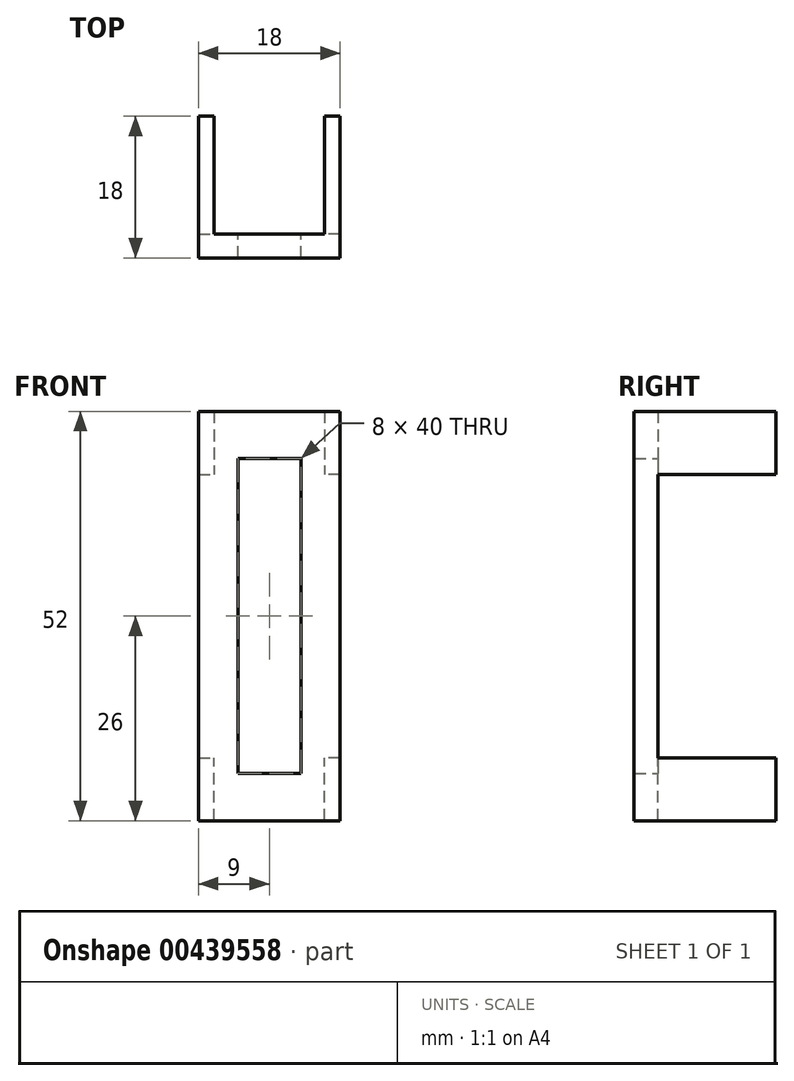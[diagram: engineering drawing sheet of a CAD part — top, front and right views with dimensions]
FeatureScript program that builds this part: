
annotation { "Feature Type Name" : "Feature", "Feature Type Description" : "" }
export const myFeature = defineFeature(function(context is Context, id is Id, definition is map)
    precondition{}
    {
        {
            var Q0;
            Q0=qCreatedBy(makeId("Front.planeOp"),FACE);
            var sketch = newSketch(context, id + "F0", { "sketchPlane" : qUnion([Q0])});
            skLineSegment(sketch, "E0.bottom", {"start": v(-9, 26) * mm, "end": v(9, 26) * mm});
            skLineSegment(sketch, "E0.top", {"start": v(-9, -26) * mm, "end": v(9, -26) * mm});
            skLineSegment(sketch, "E0.left", {"start": v(-9, 26) * mm, "end": v(-9, -26) * mm});
            skLineSegment(sketch, "E0.right", {"start": v(9, 26) * mm, "end": v(9, -26) * mm});
            skLineSegment(sketch, "E1.bottom", {"start": v(-4, 20) * mm, "end": v(4, 20) * mm});
            skLineSegment(sketch, "E1.top", {"start": v(-4, -20) * mm, "end": v(4, -20) * mm});
            skLineSegment(sketch, "E1.left", {"start": v(-4, 20) * mm, "end": v(-4, -20) * mm});
            skLineSegment(sketch, "E1.right", {"start": v(4, 20) * mm, "end": v(4, -20) * mm});
            skSolve(sketch);
        }
        {
            var Q0;
            Q0=makeQuery(id+"F0.imprint","IMPRINT",FACE,{"disambiguationData":[TD([[makeQuery(id+"F0.imprint","IMPRINT",EDGE,{"derivedFrom":sQuery(id+"F0.wireOp",EDGE,"E0.bottom")}),-1.0]])]});
            extrude(context, id + "F1", {"entities" : qUnion([Q0]), "depth" : 3 * mm, "offsetDistance" : 25 * mm});
        }
        {
            var Q0;
            Q0=makeQuery(id+"F1.opExtrude","CAP_FACE",FACE,{"disambiguationData":[OSD([sQuery(id+"F0.wireOp",EDGE,"E0.bottom"),sQuery(id+"F0.wireOp",EDGE,"E0.top"),sQuery(id+"F0.wireOp",EDGE,"E0.left"),sQuery(id+"F0.wireOp",EDGE,"E0.right")])],"isStart":true});
            var sketch = newSketch(context, id + "F2", { "sketchPlane" : qUnion([Q0])});
            skLineSegment(sketch, "E2.bottom", {"start": v(-9, 26) * mm, "end": v(-7, 26) * mm});
            skLineSegment(sketch, "E2.top", {"start": v(-9, 18) * mm, "end": v(-7, 18) * mm});
            skLineSegment(sketch, "E2.left", {"start": v(-9, 26) * mm, "end": v(-9, 18) * mm});
            skLineSegment(sketch, "E2.right", {"start": v(-7, 26) * mm, "end": v(-7, 18) * mm});
            skLineSegment(sketch, "E3.bottom", {"start": v(9, 26) * mm, "end": v(7, 26) * mm});
            skLineSegment(sketch, "E3.top", {"start": v(9, 18) * mm, "end": v(7, 18) * mm});
            skLineSegment(sketch, "E3.left", {"start": v(9, 26) * mm, "end": v(9, 18) * mm});
            skLineSegment(sketch, "E3.right", {"start": v(7, 26) * mm, "end": v(7, 18) * mm});
            skLineSegment(sketch, "E4.bottom", {"start": v(9, -26) * mm, "end": v(7, -26) * mm});
            skLineSegment(sketch, "E4.top", {"start": v(9, -18) * mm, "end": v(7, -18) * mm});
            skLineSegment(sketch, "E4.left", {"start": v(9, -26) * mm, "end": v(9, -18) * mm});
            skLineSegment(sketch, "E4.right", {"start": v(7, -26) * mm, "end": v(7, -18) * mm});
            skLineSegment(sketch, "E5.bottom", {"start": v(-9, -26) * mm, "end": v(-7, -26) * mm});
            skLineSegment(sketch, "E5.top", {"start": v(-9, -18) * mm, "end": v(-7, -18) * mm});
            skLineSegment(sketch, "E5.left", {"start": v(-9, -26) * mm, "end": v(-9, -18) * mm});
            skLineSegment(sketch, "E5.right", {"start": v(-7, -26) * mm, "end": v(-7, -18) * mm});
            skSolve(sketch);
        }
        {
            var Q0;
            Q0=makeQuery(id+"F2.imprint","IMPRINT",FACE,{"disambiguationData":[TD([[makeQuery(id+"F2.imprint","IMPRINT",EDGE,{"derivedFrom":sQuery(id+"F2.wireOp",EDGE,"E2.bottom")}),1.0]])]});
            var Q1;
            Q1=makeQuery(id+"F2.imprint","IMPRINT",FACE,{"disambiguationData":[TD([[makeQuery(id+"F2.imprint","IMPRINT",EDGE,{"derivedFrom":sQuery(id+"F2.wireOp",EDGE,"E3.bottom")}),1.0]])]});
            var Q2;
            Q2=makeQuery(id+"F2.imprint","IMPRINT",FACE,{"disambiguationData":[TD([[makeQuery(id+"F2.imprint","IMPRINT",EDGE,{"derivedFrom":sQuery(id+"F2.wireOp",EDGE,"E4.bottom")}),-1.0]])]});
            var Q3;
            Q3=makeQuery(id+"F2.imprint","IMPRINT",FACE,{"disambiguationData":[TD([[makeQuery(id+"F2.imprint","IMPRINT",EDGE,{"derivedFrom":sQuery(id+"F2.wireOp",EDGE,"E5.bottom")}),-1.0]])]});
            extrude(context, id + "F3", {"entities" : qUnion([Q0, Q1, Q2, Q3]), "operationType" : NewBodyOperationType.ADD, "depth" : 15 * mm, "offsetDistance" : 25 * mm});
        }
    });
